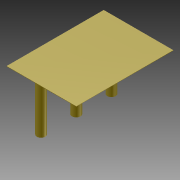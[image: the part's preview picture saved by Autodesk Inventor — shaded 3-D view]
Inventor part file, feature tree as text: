
AUTODESK INVENTOR PART (.ipt)
format: ipt  version: 2011 SP1 (Build 150282100, 282)  size: 91,136 bytes
history: native  units: in
note: dims shown in document units (in); Inventor stores cm internally (conversion verified against a paired STEP export)
features: other x14, extrude x4, sketch x4
ambient origin geometry x8: Origin, YZ Plane, XZ Plane, XY Plane, X Axis, Y Axis, Z Axis, Center Point
bodies: Solid1 (feature_tree)
feature tree (22):
  extrude  "Extrusion1"  Depth=0.156in TaperAngle=0.0deg
  extrude  "Extrusion2"  Depth=0.156in TaperAngle=0.0deg
  extrude  "Extrusion3"  [1 undecoded]
  extrude  "Extrusion4"  [1 undecoded]
  other  "right_vertical_trmnls_XY"
  other  "right_vertical_trmnls_YZ"
  other  "right_vertical_trmnls_ZX"
  other  "right_vertical_trmnls_X"
  other  "right_vertical_trmnls_Y"
  other  "right_vertical_trmnls_Z"
  other  "right_vertical_trmnls_Center"
  other  "stright_trmnls_XY"
  other  "stright_trmnls_YZ"
  other  "stright_trmnls_ZX"
  other  "stright_trmnls_X"
  other  "stright_trmnls_Y"
  other  "stright_trmnls_Z"
  other  "stright_trmnls_Center"
  sketch  "Sketch_1"  dims[d0=0.001in d1=0.0in d2=0.156in d3=0.0in]
  sketch  "Sketch_2"  dims[d4=0.156in d5=0.0in d6=0.156in d7=0.0in]
  sketch  "Sketch_3"
  sketch  "Sketch_4"
note: 2 required parameter values undecoded (feature->parameter linkage not recoverable at this tier; creation-order binding heuristic only, values carry confidence <= 0.55)
